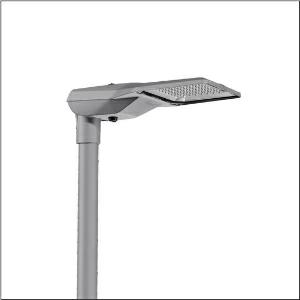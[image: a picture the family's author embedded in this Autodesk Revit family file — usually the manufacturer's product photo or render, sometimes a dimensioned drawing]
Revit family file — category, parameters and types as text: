
# Revit family: streetlight_sl_21_iq_midi___st1_0a_5xe3d51y08mb_fe0f
name_source: partatom
category: Lighting Fixtures
units: mm (PartAtom-declared; Revit-internal decimal feet)

## family parameters
Cut with Voids When Loaded = No
Host = Face
Light Source = No
Part Type = Normal
Room Calculation Point = No
Round Connector Dimension = Use Diameter
Shared = No

## types (1)
- --- (1 x LED, 16100 lm, 129.3 W, 3000K)
    Apparent Load = 129 VA
    CIE Flux Codes = 37 72 97 100 100
    Color Rendering = 80
    Color Temperature = 3000K
    Default Elevation = 1800 mm
    Description = Streetlight SL 21 iQ midi, mast luminaire, primary light control with lens, of PMMA, primary optical cover: cover, of toughened safety glass, transparent, light distribution: ST1.0a, light emission: direct distribution, primary light characteristic: asymmetric, installation type: post-top, side-entry, LED, High Power LED, rated luminous flux: 16.100lm, luminous efficacy: 125lm/W, light colour: 830, colour temperature: 3000K, control: presetting dimming logarithmic, Street-Remote, Auto-Match, Temp-Guard, Lumen-Switch, Night-Set, Smart-Wire, Light-Fading, Desk-Remote (wireless, voltage-free reading and setting of iQ features in the workshop via application-optimized NFC function/RFID function), optimised constant luminous flux control (CLO 2.0), mains connection: 230..240V, AC, 50/60Hz, start of lifetime: 129W, end of service life: 142W, reduction: 56W, luminaire housing, of diecast aluminium, powder-coated, Siteco® metallic grey (DB 702S), corrosivity category C5 mid according to DIN EN ISO 12944, please order mast flange separately, inclination adjustable: 0°, 5°, 10°, 15°, sealing non-destructively replaceable, multi-level sealing system, length: 644mm, width: 335mm, height: 110mm, mast flange for spigot size: 42mm (side-entry): 5XC10008XM4, 60/48mm (side-entry/post-top): 5XC10108XM2, 76/60mm (side-entry/post-top): 5XC10108XM1, Smart Interface below and above, protection rating (complete): IP66, insulation class (complete): insulation class II (safety insulation), certification: CE, ENEC, ENEC+, VDE, impact resistance: IK09, permissible operating ambient temperature for outdoor applications: -40..+50°C, standard-compliant lighting for roads and squares, packaging unit: 1 piece

Light Distribution: ST1.0a
    Height = 111 mm
    Lamp = 1 x LED
    Lamp Light Flux = 16100 lm
    Lamp Power = 129.3 W
    Lamp count = 1
    Length = 644 mm
    Luminous efficacy = 125 lm/W
    Manufacturer = Siteco
    ModVariant = No
    Model = 5XE3D51Y08MB
    Number of Poles = 1
    OnlyDefault = Yes
    Power Factor = 1
    Product Name = Streetlight SL 21 iQ midi | ST1.0a
    Product group = mast luminaire | pylon top
    ProductGroupID = 6100
    Protection Class = Protection class II
    Protection Degree = IP 66
    RLX_Detail_Level = 1
    RLX_Emergency_Light_Flux = 0 lm
    RLX_Emergency_Type = 0
    RLX_Emergency_Type_DB = No
    RlxData = <blob elided: 91213 chars, md5=fb36302e>
    Socket = socket
    Standby Power = 0 W
    System Light Flux = 16100 lm
    System Power = 129 W
    Type Comments = factory setting: luminous flux: 100 % | dim-lin: 254 | 672 mA
    Type Image = l_1004304.jpg
    URL = http://relux.com
    VarID = @adj_044531
    Voltage = 0 V
    Weight = 0.00 kg
    Width = 336 mm

## geometry (parser evidence)
native form markers: Blend x4, Sweep x11
no freeform markers — native parametric forms only
